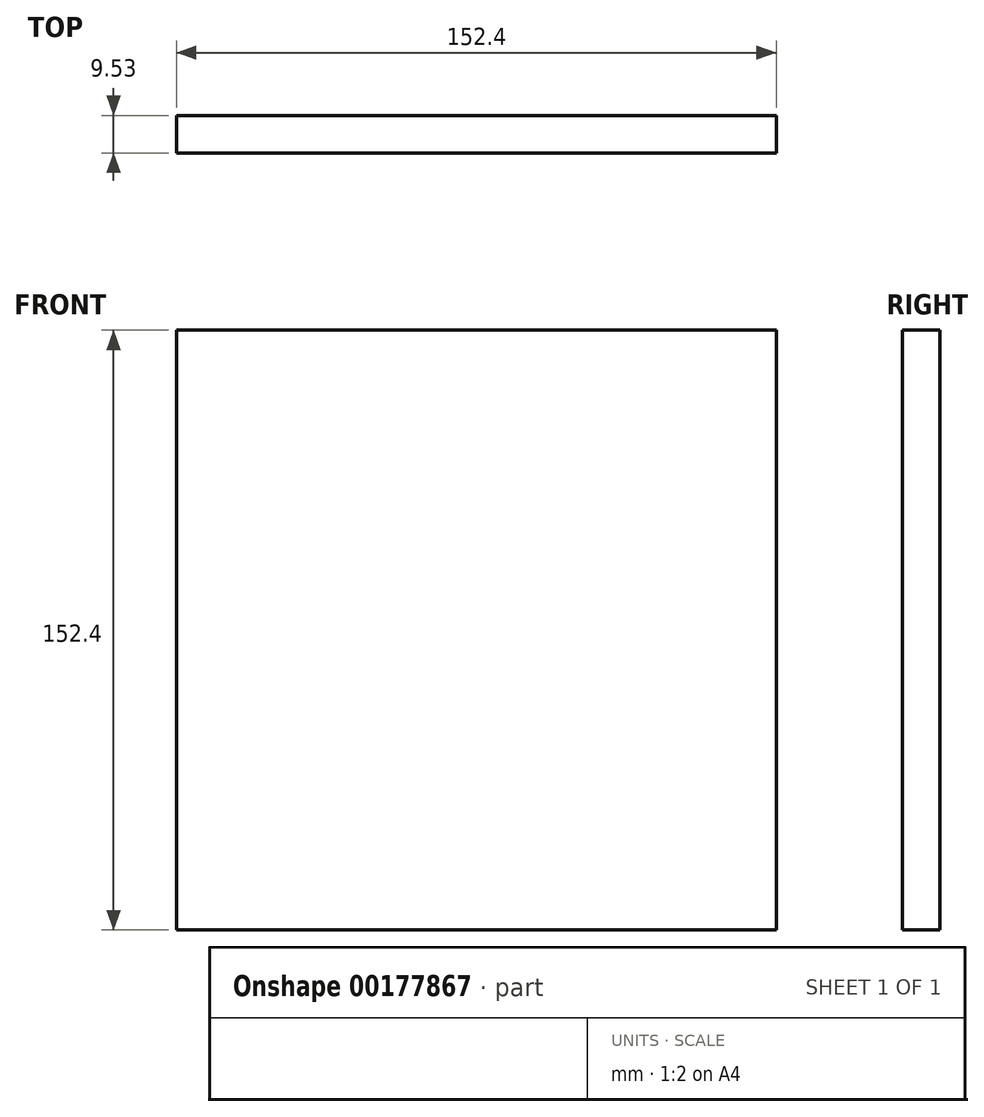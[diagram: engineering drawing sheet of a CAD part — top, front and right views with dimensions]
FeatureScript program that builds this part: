
annotation { "Feature Type Name" : "Feature", "Feature Type Description" : "" }
export const myFeature = defineFeature(function(context is Context, id is Id, definition is map)
    precondition{}
    {
        {
            var Q0;
            Q0=qCreatedBy(makeId("Front.planeOp"),FACE);
            var sketch = newSketch(context, id + "F0", { "sketchPlane" : qUnion([Q0])});
            skLineSegment(sketch, "E0.bottom", {"start": v(-73.88, 78.36) * mm, "end": v(78.52, 78.36) * mm});
            skLineSegment(sketch, "E0.top", {"start": v(-73.88, -74.04) * mm, "end": v(78.52, -74.04) * mm});
            skLineSegment(sketch, "E0.left", {"start": v(-73.88, 78.36) * mm, "end": v(-73.88, -74.04) * mm});
            skLineSegment(sketch, "E0.right", {"start": v(78.52, 78.36) * mm, "end": v(78.52, -74.04) * mm});
            skSolve(sketch);
        }
        {
            var Q0;
            Q0 = qSketchRegion(id + "F0", true);
            extrude(context, id + "F1", {"entities" : qUnion([Q0]), "depth" : 9.52 * mm});
        }
    });
